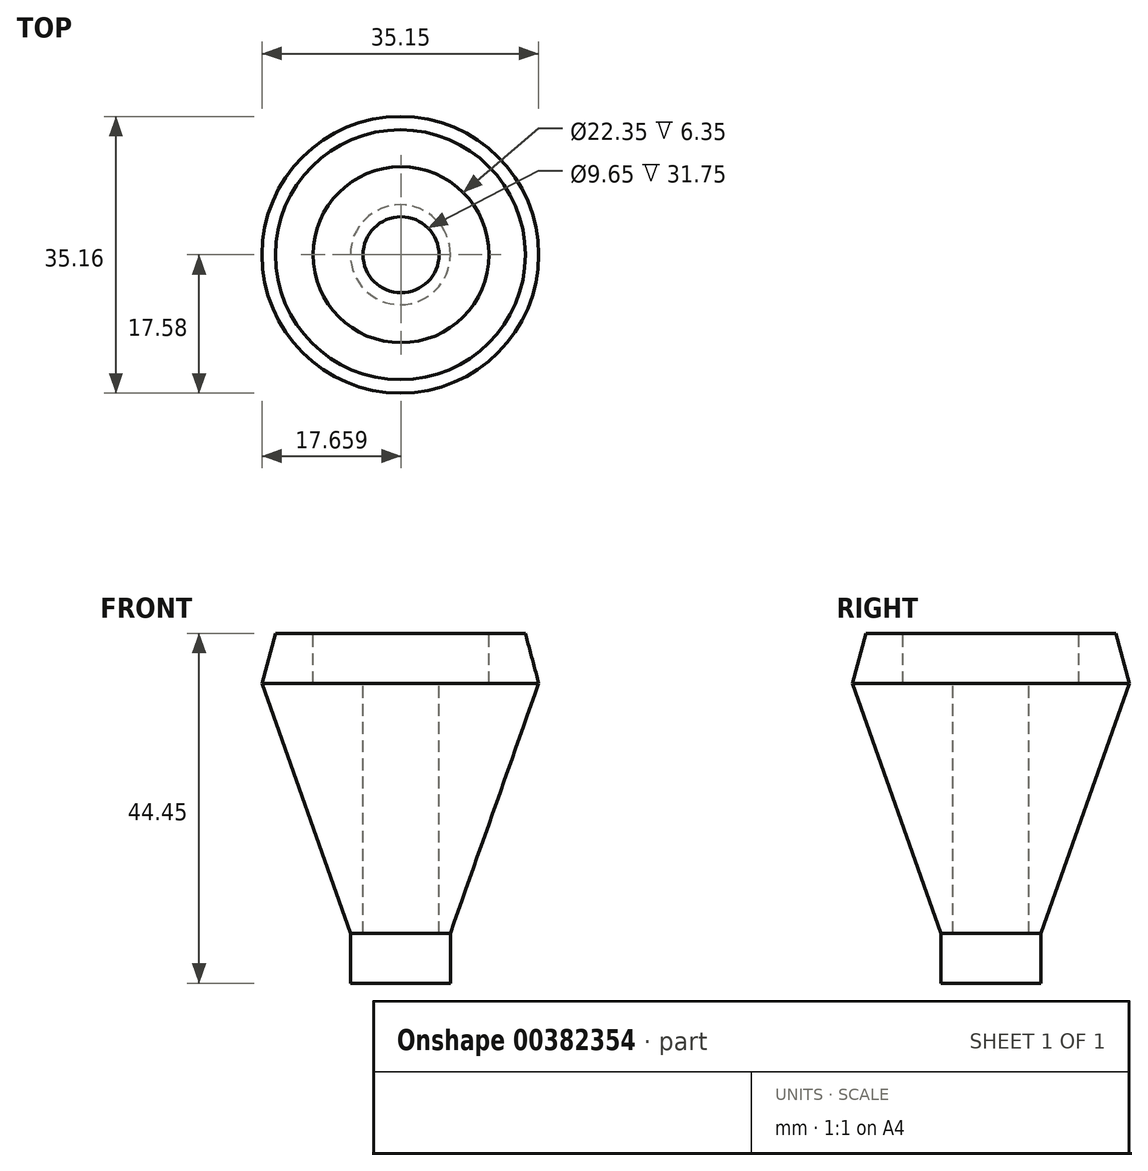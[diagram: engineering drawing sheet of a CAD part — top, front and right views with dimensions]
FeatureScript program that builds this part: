
annotation { "Feature Type Name" : "Feature", "Feature Type Description" : "" }
export const myFeature = defineFeature(function(context is Context, id is Id, definition is map)
    precondition{}
    {
        {
            var Q0;
            Q0=qCreatedBy(makeId("Front.planeOp"),FACE);
            var sketch = newSketch(context, id + "F0", { "sketchPlane" : qUnion([Q0])});
            skLineSegment(sketch, "E0", {"start": v(-10.64, -24.26) * mm, "end": v(-10.64, -17.9) * mm});
            skLineSegment(sketch, "E1", {"start": v(-10.64, -17.9) * mm, "end": v(0.59, 13.84) * mm});
            skLineSegment(sketch, "E2", {"start": v(0.59, 13.84) * mm, "end": v(-1.11, 20.2) * mm});
            skLineSegment(sketch, "E3", {"start": v(0.59, 33.37) * mm, "end": v(0.59, 13.84) * mm});
            skLineSegment(sketch, "E4", {"start": v(-16.99, 20.2) * mm, "end": v(-16.99, -24.26) * mm});
            skLineSegment(sketch, "E5", {"start": v(-16.99, 20.2) * mm, "end": v(-1.11, 20.2) * mm});
            skLineSegment(sketch, "E6", {"start": v(-16.99, -24.26) * mm, "end": v(-10.64, -24.26) * mm});
            skSolve(sketch);
        }
        {
            var Q0;
            {var subQ1=sQuery(id+"F0.wireOp",EDGE,"E0");Q0=makeQuery(id+"F0.imprint","IMPRINT",FACE,{"disambiguationData":[TD([[makeQuery(id+"F0.imprint","IMPRINT",EDGE,{"derivedFrom":subQ1}),1.0]])]});}
            var Q1;
            Q1=sQuery(id+"F0.wireOp",EDGE,"E4");
            revolve(context, id + "F1", {"entities" : qUnion([Q0]), "axis" : qUnion([Q1]), "revolveType" : RevolveType.FULL});
        }
        {
            var Q0;
            Q0=makeQuery(id+"F1.opRevolve","SWEPT_FACE",FACE,{"disambiguationData":[OSD([sQuery(id+"F0.wireOp",EDGE,"E5")])]});
            var sketch = newSketch(context, id + "F2", { "sketchPlane" : qUnion([Q0])});
            skCircle(sketch, "E7", {"center": v(-16.9, 0) * mm, "radius": 11.18 * mm});
            skCircle(sketch, "E8", {"center": v(-16.9, 0) * mm, "radius": 4.83 * mm});
            skSolve(sketch);
        }
        {
            var Q0;
            Q0=makeQuery(id+"F2.imprint","IMPRINT",FACE,{"disambiguationData":[TD([[makeQuery(id+"F2.imprint","IMPRINT",EDGE,{"derivedFrom":sQuery(id+"F2.wireOp",EDGE,"E8")}),1.0]])]});
            extrude(context, id + "F3", {"entities" : qUnion([Q0]), "operationType" : NewBodyOperationType.REMOVE, "oppositeDirection" : true, "depth" : 38.1 * mm});
        }
        {
            var Q0;
            Q0=makeQuery(id+"F2.imprint","IMPRINT",FACE,{"disambiguationData":[TD([[makeQuery(id+"F2.imprint","IMPRINT",EDGE,{"derivedFrom":sQuery(id+"F2.wireOp",EDGE,"E7")}),1.0]])]});
            extrude(context, id + "F4", {"entities" : qUnion([Q0]), "operationType" : NewBodyOperationType.REMOVE, "oppositeDirection" : true, "depth" : 6.35 * mm});
        }
    });
